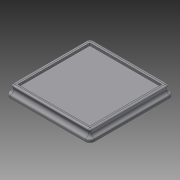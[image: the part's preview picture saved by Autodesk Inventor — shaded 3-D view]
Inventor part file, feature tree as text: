
AUTODESK INVENTOR PART (.ipt)
format: ipt  version: 2015 SP1 (Build 190203100, 203)  size: 150,528 bytes
history: native  units: mm
features: sketch x4, extrude x3, sweep x1
ambient origin geometry x8: Origin, YZ Plane, XZ Plane, XY Plane, X Axis, Y Axis, Z Axis, Center Point
bodies: Solid1 (feature_tree)
feature tree (8):
  sketch  "Sketch2"  dims[d2=380.0mm d3=0.2mm]
  sweep  "Sweep1"
  extrude  "Extrusion1"  Depth=0.2mm
  extrude  "Extrusion2"  Depth=50.0mm TaperAngle=0.0deg
  extrude  "Extrusion3"  Depth=2.5mm
  sketch  "Sketch1"  dims[d0=50.0mm d1=380.0mm]
  sketch  "Sketch3"  dims[d4=0.0mm d5=0.0mm d6=50.0mm d7=0.0mm]
  sketch  "Sketch4"  dims[d8=360.0mm d9=360.0mm d10=10.0mm d11=0.0mm d12=365.0mm d13=365.0mm d14=2.5mm d15=0.0mm]
